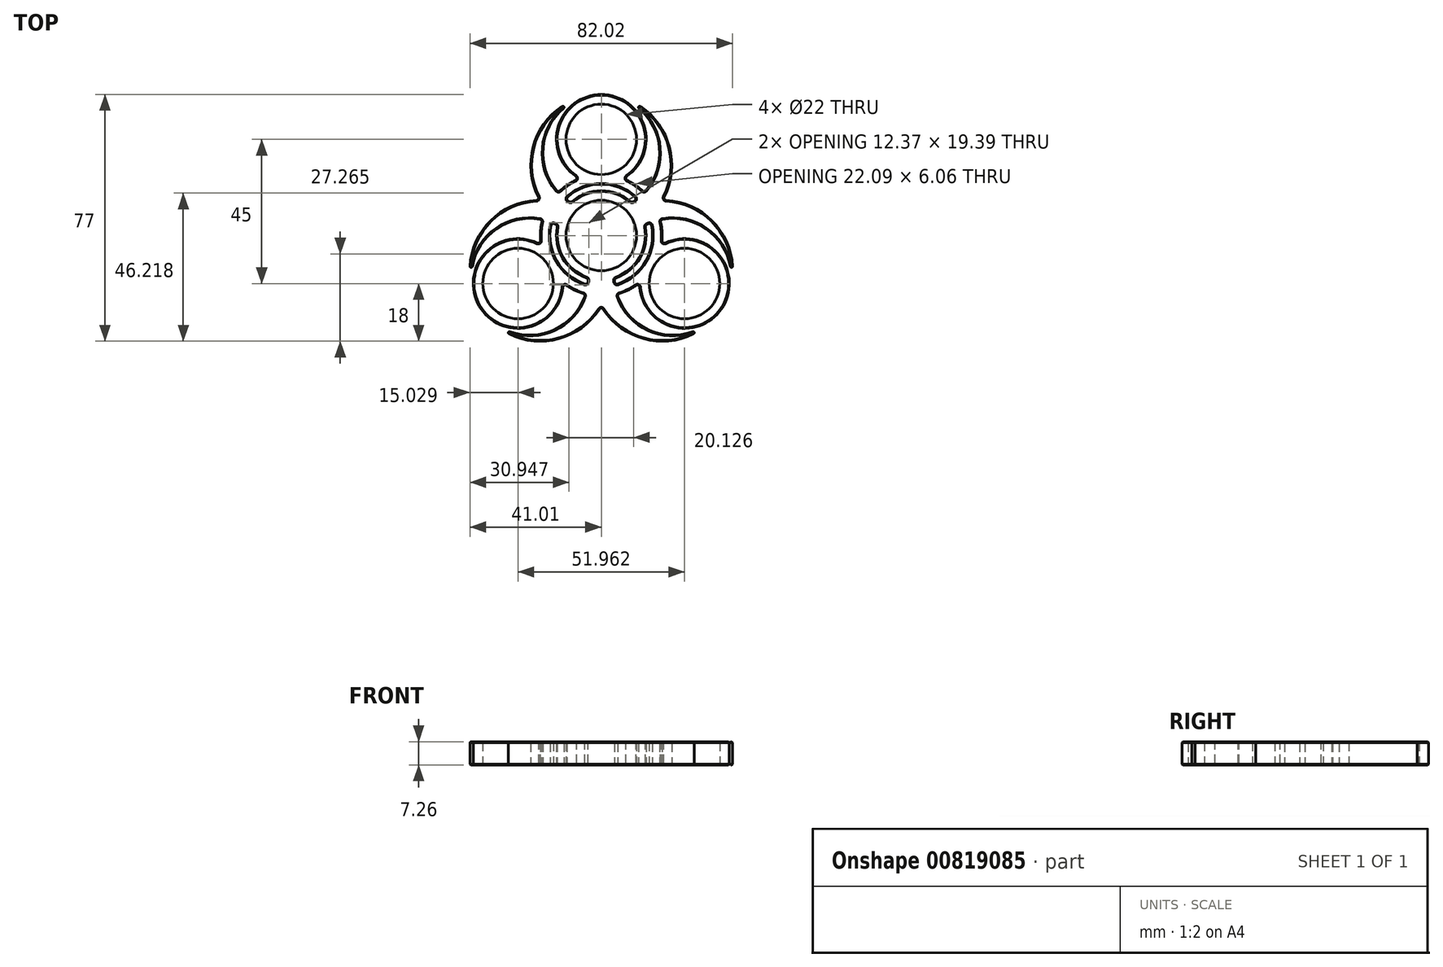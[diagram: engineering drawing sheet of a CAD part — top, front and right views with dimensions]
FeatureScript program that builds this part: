
annotation { "Feature Type Name" : "Feature", "Feature Type Description" : "" }
export const myFeature = defineFeature(function(context is Context, id is Id, definition is map)
    precondition{}
    {
        {
            var Q0;
            Q0=qCreatedBy(makeId("Top.planeOp"),FACE);
            var sketch = newSketch(context, id + "F0", { "sketchPlane" : qUnion([Q0])});
            skCircle(sketch, "E0", {"center": v(0, 0) * mm, "radius": 14 * mm});
            skCircle(sketch, "E1", {"center": v(0, 0) * mm, "radius": 11 * mm});
            skCircle(sketch, "E2", {"center": v(0, 30) * mm, "radius": 14 * mm});
            skCircle(sketch, "E3", {"center": v(0, 30) * mm, "radius": 11 * mm});
            skCircle(sketch, "E4", {"center": v(0, 0) * mm, "radius": 19 * mm});
            skCircle(sketch, "E5", {"center": v(0, 0) * mm, "radius": 16 * mm});
            skCircle(sketch, "E6.1.0", {"center": v(-25.98, -15) * mm, "radius": 14 * mm});
            skCircle(sketch, "E6.1.1", {"center": v(-25.98, -15) * mm, "radius": 11 * mm});
            skCircle(sketch, "E6.2.0", {"center": v(25.98, -15) * mm, "radius": 14 * mm});
            skCircle(sketch, "E6.2.1", {"center": v(25.98, -15) * mm, "radius": 11 * mm});
            skSolve(sketch);
        }
        {
            var Q0;
            Q0=makeQuery(id+"F0.imprint","IMPRINT",FACE,{"disambiguationData":[TD([[makeQuery(id+"F0.imprint","IMPRINT",EDGE,{"derivedFrom":sQuery(id+"F0.wireOp",EDGE,"E0")}),1.0]])]});
            var Q1;
            {var subQ0=sQuery(id+"F0.wireOp",EDGE,"E4");var subQ1=sQuery(id+"F0.wireOp",EDGE,"E2");var subQ2=makeQuery(id+"F0.imprint","INTERSECT",VERTEX,{"disambiguationData":[OD(1.0)],"derivedFrom":[subQ1,subQ0]});Q1=makeQuery(id+"F0.imprint","IMPRINT",FACE,{"disambiguationData":[TD([[makeQuery(id+"F0.imprint","IMPRINT",EDGE,{"disambiguationData":[TD([[subQ2,1.0]])],"derivedFrom":subQ1}),-1.0]])]});}
            var Q2;
            {var subQ0=sQuery(id+"F0.wireOp",EDGE,"E4");var subQ1=sQuery(id+"F0.wireOp",EDGE,"E2");var subQ2=makeQuery(id+"F0.imprint","INTERSECT",VERTEX,{"disambiguationData":[OD(0.0)],"derivedFrom":[subQ1,subQ0]});Q2=makeQuery(id+"F0.imprint","IMPRINT",FACE,{"disambiguationData":[TD([[makeQuery(id+"F0.imprint","IMPRINT",EDGE,{"disambiguationData":[TD([[subQ2,-1.0]])],"derivedFrom":subQ1}),-1.0]])]});}
            var Q3;
            {var subQ0=sQuery(id+"F0.wireOp",EDGE,"E6.1.0");var subQ1=sQuery(id+"F0.wireOp",EDGE,"E4");var subQ2=makeQuery(id+"F0.imprint","INTERSECT",VERTEX,{"disambiguationData":[OD(1.0)],"derivedFrom":[subQ1,subQ0]});Q3=makeQuery(id+"F0.imprint","IMPRINT",FACE,{"disambiguationData":[TD([[makeQuery(id+"F0.imprint","IMPRINT",EDGE,{"disambiguationData":[TD([[subQ2,-1.0]])],"derivedFrom":subQ1}),1.0]])]});}
            var Q4;
            {var subQ3=sQuery(id+"F0.wireOp",EDGE,"E6.1.1");Q4=makeQuery(id+"F0.imprint","IMPRINT",FACE,{"disambiguationData":[TD([[makeQuery(id+"F0.imprint","IMPRINT",EDGE,{"derivedFrom":subQ3}),-1.0]])]});}
            var Q5;
            {var subQ0=sQuery(id+"F0.wireOp",EDGE,"E6.1.0");var subQ1=sQuery(id+"F0.wireOp",EDGE,"E4");var subQ2=makeQuery(id+"F0.imprint","INTERSECT",VERTEX,{"disambiguationData":[OD(0.0)],"derivedFrom":[subQ1,subQ0]});Q5=makeQuery(id+"F0.imprint","IMPRINT",FACE,{"disambiguationData":[TD([[makeQuery(id+"F0.imprint","IMPRINT",EDGE,{"disambiguationData":[TD([[subQ2,-1.0]])],"derivedFrom":subQ1}),1.0]])]});}
            var Q6;
            {var subQ3=sQuery(id+"F0.wireOp",EDGE,"E6.2.1");Q6=makeQuery(id+"F0.imprint","IMPRINT",FACE,{"disambiguationData":[TD([[makeQuery(id+"F0.imprint","IMPRINT",EDGE,{"derivedFrom":subQ3}),-1.0]])]});}
            var Q7;
            {var subQ0=sQuery(id+"F0.wireOp",EDGE,"E6.2.0");var subQ1=sQuery(id+"F0.wireOp",EDGE,"E4");var subQ2=makeQuery(id+"F0.imprint","INTERSECT",VERTEX,{"disambiguationData":[OD(0.0)],"derivedFrom":[subQ1,subQ0]});Q7=makeQuery(id+"F0.imprint","IMPRINT",FACE,{"disambiguationData":[TD([[makeQuery(id+"F0.imprint","IMPRINT",EDGE,{"disambiguationData":[TD([[subQ2,-1.0]])],"derivedFrom":subQ1}),1.0]])]});}
            var Q8;
            {var subQ4=sQuery(id+"F0.wireOp",EDGE,"E3");Q8=makeQuery(id+"F0.imprint","IMPRINT",FACE,{"disambiguationData":[TD([[makeQuery(id+"F0.imprint","IMPRINT",EDGE,{"derivedFrom":subQ4}),-1.0]])]});}
            var Q9;
            {var subQ0=sQuery(id+"F0.wireOp",EDGE,"E4");var subQ1=sQuery(id+"F0.wireOp",EDGE,"E2");var subQ2=makeQuery(id+"F0.imprint","INTERSECT",VERTEX,{"disambiguationData":[OD(0.0)],"derivedFrom":[subQ1,subQ0]});Q9=makeQuery(id+"F0.imprint","IMPRINT",FACE,{"disambiguationData":[TD([[makeQuery(id+"F0.imprint","IMPRINT",EDGE,{"disambiguationData":[TD([[subQ2,-1.0]])],"derivedFrom":subQ1}),1.0]])]});}
            extrude(context, id + "F1", {"entities" : qUnion([Q0, Q1, Q2, Q3, Q4, Q5, Q6, Q7, Q8, Q9]), "endBound" : BoundingType.SYMMETRIC, "depth" : 7.25 * mm, "offsetDistance" : 25.4 * mm});
        }
        {
            var Q0;
            Q0=qCreatedBy(makeId("Top.planeOp"),FACE);
            var sketch = newSketch(context, id + "F2", { "sketchPlane" : qUnion([Q0])});
            skArc(sketch, "E7", {"start": v(-11.76, 39.7) * mm, "mid": v(0, 7.55) * mm, "end": v(11.76, 39.7) * mm});
            skLineSegment(sketch, "E8", {"start": v(12.89, 12.89) * mm, "end": v(47.12, 47.12) * mm, "construction": true});
            skArc(sketch, "E9", {"start": v(-12.2, 40.3) * mm, "mid": v(-21.42, 27) * mm, "end": v(-19.05, 11) * mm});
            skArc(sketch, "E10", {"start": v(12.2, 40.3) * mm, "mid": v(11.7, 40.21) * mm, "end": v(11.76, 39.7) * mm});
            skArc(sketch, "E11", {"start": v(-11.76, 39.7) * mm, "mid": v(-11.7, 40.21) * mm, "end": v(-12.2, 40.3) * mm});
            skArc(sketch, "E12.1.0", {"start": v(-28.5, -30.03) * mm, "mid": v(-6.54, -3.77) * mm, "end": v(-40.26, -9.67) * mm});
            skArc(sketch, "E12.1.1", {"start": v(-28.8, -30.72) * mm, "mid": v(-12.67, -32.06) * mm, "end": v(0, -22) * mm});
            skArc(sketch, "E12.1.2", {"start": v(-41, -9.58) * mm, "mid": v(-40.68, -9.98) * mm, "end": v(-40.26, -9.67) * mm});
            skArc(sketch, "E12.1.3", {"start": v(-28.5, -30.03) * mm, "mid": v(-28.98, -30.24) * mm, "end": v(-28.8, -30.72) * mm});
            skArc(sketch, "E12.2.0", {"start": v(40.26, -9.67) * mm, "mid": v(6.54, -3.77) * mm, "end": v(28.5, -30.03) * mm});
            skArc(sketch, "E12.2.1", {"start": v(41, -9.58) * mm, "mid": v(34.1, 5.05) * mm, "end": v(19.05, 11) * mm});
            skArc(sketch, "E12.2.2", {"start": v(28.8, -30.72) * mm, "mid": v(28.98, -30.24) * mm, "end": v(28.5, -30.03) * mm});
            skArc(sketch, "E12.2.3", {"start": v(40.26, -9.67) * mm, "mid": v(40.68, -9.98) * mm, "end": v(41, -9.58) * mm});
            skPoint(sketch, "E12.center", {"position": v(0, 0) * mm});
            skArc(sketch, "E13.trimOffspring", {"start": v(-19.05, 11) * mm, "mid": v(-34.1, 5.05) * mm, "end": v(-41, -9.58) * mm});
            skArc(sketch, "E14.trimOffspring", {"start": v(0, -22) * mm, "mid": v(12.67, -32.06) * mm, "end": v(28.8, -30.72) * mm});
            skArc(sketch, "E15.trimOffspring", {"start": v(19.05, 11) * mm, "mid": v(21.42, 27) * mm, "end": v(12.2, 40.3) * mm});
            skSolve(sketch);
        }
        {
            var Q0;
            Q0=makeQuery(id+"F2.imprint","IMPRINT",FACE,{"disambiguationData":[TD([[makeQuery(id+"F2.imprint","IMPRINT",EDGE,{"derivedFrom":sQuery(id+"F2.wireOp",EDGE,"E7")}),-1.0]])]});
            extrude(context, id + "F3", {"entities" : qUnion([Q0]), "operationType" : NewBodyOperationType.ADD, "endBound" : BoundingType.SYMMETRIC, "depth" : 7.25 * mm, "offsetDistance" : 25 * mm});
        }
        {
            var Q0;
            Q0=makeQuery(id+"F0.imprint","IMPRINT",FACE,{"disambiguationData":[TD([[makeQuery(id+"F0.imprint","IMPRINT",EDGE,{"derivedFrom":sQuery(id+"F0.wireOp",EDGE,"E1")}),1.0]])]});
            extrude(context, id + "F4", {"entities" : qUnion([Q0]), "operationType" : NewBodyOperationType.REMOVE, "endBound" : BoundingType.SYMMETRIC, "depth" : 8 * mm, "offsetDistance" : 25 * mm});
        }
        {
            var Q0;
            {var subQ0=sQuery(id+"F0.wireOp",EDGE,"E4");var subQ1=sQuery(id+"F0.wireOp",EDGE,"E2");Q0=makeQuery(id+"F1.opExtrude","SWEPT_EDGE",EDGE,{"disambiguationData":[OSD([subQ1,subQ0]),TDD([makeQuery(id+"F0.imprint","INTERSECT",VERTEX,{"disambiguationData":[OD(1.0)],"derivedFrom":[subQ1,subQ0]})])]});}
            var Q1;
            {var subQ0=sQuery(id+"F0.wireOp",EDGE,"E4");var subQ1=sQuery(id+"F0.wireOp",EDGE,"E2");Q1=makeQuery(id+"F1.opExtrude","SWEPT_EDGE",EDGE,{"disambiguationData":[OSD([subQ1,subQ0]),TDD([makeQuery(id+"F0.imprint","INTERSECT",VERTEX,{"disambiguationData":[OD(0.0)],"derivedFrom":[subQ1,subQ0]})])]});}
            var Q2;
            {var subQ0=sQuery(id+"F0.wireOp",EDGE,"E4");Q2=makeQuery(id+"F3.boolean.opBoolean","INTERSECT",EDGE,{"derivedFrom":[makeQuery(id+"F1.opExtrude","SWEPT_FACE",FACE,{"disambiguationData":[OSD([subQ0]),TDD([makeQuery(id+"F0.imprint","IMPRINT",EDGE,{"disambiguationData":[TD([[makeQuery(id+"F0.imprint","INTERSECT",VERTEX,{"disambiguationData":[OD(0.0)],"derivedFrom":[sQuery(id+"F0.wireOp",EDGE,"E2"),subQ0]}),-1.0]])],"derivedFrom":subQ0})])]}),makeQuery(id+"F3.opExtrude","SWEPT_FACE",FACE,{"disambiguationData":[OSD([sQuery(id+"F2.wireOp",EDGE,"E7")])]})]});}
            var Q3;
            {var subQ0=sQuery(id+"F0.wireOp",EDGE,"E4");Q3=makeQuery(id+"F3.boolean.opBoolean","INTERSECT",EDGE,{"derivedFrom":[makeQuery(id+"F1.opExtrude","SWEPT_FACE",FACE,{"disambiguationData":[OSD([subQ0]),TDD([makeQuery(id+"F0.imprint","IMPRINT",EDGE,{"disambiguationData":[TD([[makeQuery(id+"F0.imprint","INTERSECT",VERTEX,{"disambiguationData":[OD(0.0)],"derivedFrom":[sQuery(id+"F0.wireOp",EDGE,"E2"),subQ0]}),-1.0]])],"derivedFrom":subQ0})])]}),makeQuery(id+"F3.opExtrude","SWEPT_FACE",FACE,{"disambiguationData":[OSD([sQuery(id+"F2.wireOp",EDGE,"E12.1.0")])]})]});}
            var Q4;
            Q4=makeQuery(id+"F3.boolean.opBoolean","INTERSECT",EDGE,{"disambiguationData":[OD(0.0)],"derivedFrom":[makeQuery(id+"F1.opExtrude","SWEPT_FACE",FACE,{"disambiguationData":[OSD([sQuery(id+"F0.wireOp",EDGE,"E0")])]}),makeQuery(id+"F3.opExtrude","SWEPT_FACE",FACE,{"disambiguationData":[OSD([sQuery(id+"F2.wireOp",EDGE,"E12.1.0")])]})]});
            var Q5;
            Q5=makeQuery(id+"F3.boolean.opBoolean","INTERSECT",EDGE,{"disambiguationData":[OD(0.0)],"derivedFrom":[makeQuery(id+"F1.opExtrude","SWEPT_FACE",FACE,{"disambiguationData":[OSD([sQuery(id+"F0.wireOp",EDGE,"E5")])]}),makeQuery(id+"F3.opExtrude","SWEPT_FACE",FACE,{"disambiguationData":[OSD([sQuery(id+"F2.wireOp",EDGE,"E7")])]})]});
            var Q6;
            Q6=makeQuery(id+"F3.boolean.opBoolean","INTERSECT",EDGE,{"disambiguationData":[OD(0.0)],"derivedFrom":[makeQuery(id+"F1.opExtrude","SWEPT_FACE",FACE,{"disambiguationData":[OSD([sQuery(id+"F0.wireOp",EDGE,"E5")])]}),makeQuery(id+"F3.opExtrude","SWEPT_FACE",FACE,{"disambiguationData":[OSD([sQuery(id+"F2.wireOp",EDGE,"E12.1.0")])]})]});
            var Q7;
            Q7=makeQuery(id+"F3.boolean.opBoolean","INTERSECT",EDGE,{"disambiguationData":[OD(1.0)],"derivedFrom":[makeQuery(id+"F1.opExtrude","SWEPT_FACE",FACE,{"disambiguationData":[OSD([sQuery(id+"F0.wireOp",EDGE,"E5")])]}),makeQuery(id+"F3.opExtrude","SWEPT_FACE",FACE,{"disambiguationData":[OSD([sQuery(id+"F2.wireOp",EDGE,"E7")])]})]});
            var Q8;
            Q8=makeQuery(id+"F3.boolean.opBoolean","INTERSECT",EDGE,{"disambiguationData":[OD(1.0)],"derivedFrom":[makeQuery(id+"F1.opExtrude","SWEPT_FACE",FACE,{"disambiguationData":[OSD([sQuery(id+"F0.wireOp",EDGE,"E0")])]}),makeQuery(id+"F3.opExtrude","SWEPT_FACE",FACE,{"disambiguationData":[OSD([sQuery(id+"F2.wireOp",EDGE,"E7")])]})]});
            var Q9;
            Q9=makeQuery(id+"F3.boolean.opBoolean","INTERSECT",EDGE,{"disambiguationData":[OD(1.0)],"derivedFrom":[makeQuery(id+"F1.opExtrude","SWEPT_FACE",FACE,{"disambiguationData":[OSD([sQuery(id+"F0.wireOp",EDGE,"E0")])]}),makeQuery(id+"F3.opExtrude","SWEPT_FACE",FACE,{"disambiguationData":[OSD([sQuery(id+"F2.wireOp",EDGE,"E12.2.0")])]})]});
            var Q10;
            Q10=makeQuery(id+"F3.boolean.opBoolean","INTERSECT",EDGE,{"disambiguationData":[OD(1.0)],"derivedFrom":[makeQuery(id+"F1.opExtrude","SWEPT_FACE",FACE,{"disambiguationData":[OSD([sQuery(id+"F0.wireOp",EDGE,"E5")])]}),makeQuery(id+"F3.opExtrude","SWEPT_FACE",FACE,{"disambiguationData":[OSD([sQuery(id+"F2.wireOp",EDGE,"E12.2.0")])]})]});
            var Q11;
            {var subQ0=sQuery(id+"F0.wireOp",EDGE,"E4");Q11=makeQuery(id+"F3.boolean.opBoolean","INTERSECT",EDGE,{"derivedFrom":[makeQuery(id+"F1.opExtrude","SWEPT_FACE",FACE,{"disambiguationData":[OSD([subQ0]),TDD([makeQuery(id+"F0.imprint","IMPRINT",EDGE,{"disambiguationData":[TD([[makeQuery(id+"F0.imprint","INTERSECT",VERTEX,{"disambiguationData":[OD(1.0)],"derivedFrom":[sQuery(id+"F0.wireOp",EDGE,"E2"),subQ0]}),1.0]])],"derivedFrom":subQ0})])]}),makeQuery(id+"F3.opExtrude","SWEPT_FACE",FACE,{"disambiguationData":[OSD([sQuery(id+"F2.wireOp",EDGE,"E7")])]})]});}
            var Q12;
            {var subQ0=sQuery(id+"F0.wireOp",EDGE,"E4");Q12=makeQuery(id+"F3.boolean.opBoolean","INTERSECT",EDGE,{"derivedFrom":[makeQuery(id+"F1.opExtrude","SWEPT_FACE",FACE,{"disambiguationData":[OSD([subQ0]),TDD([makeQuery(id+"F0.imprint","IMPRINT",EDGE,{"disambiguationData":[TD([[makeQuery(id+"F0.imprint","INTERSECT",VERTEX,{"disambiguationData":[OD(1.0)],"derivedFrom":[sQuery(id+"F0.wireOp",EDGE,"E2"),subQ0]}),1.0]])],"derivedFrom":subQ0})])]}),makeQuery(id+"F3.opExtrude","SWEPT_FACE",FACE,{"disambiguationData":[OSD([sQuery(id+"F2.wireOp",EDGE,"E12.2.0")])]})]});}
            var Q13;
            {var subQ0=sQuery(id+"F0.wireOp",EDGE,"E6.2.0");var subQ1=sQuery(id+"F0.wireOp",EDGE,"E4");Q13=makeQuery(id+"F1.opExtrude","SWEPT_EDGE",EDGE,{"disambiguationData":[OSD([subQ1,subQ0]),TDD([makeQuery(id+"F0.imprint","INTERSECT",VERTEX,{"disambiguationData":[OD(1.0)],"derivedFrom":[subQ1,subQ0]})])]});}
            var Q14;
            {var subQ0=sQuery(id+"F0.wireOp",EDGE,"E6.2.0");var subQ1=sQuery(id+"F0.wireOp",EDGE,"E4");Q14=makeQuery(id+"F1.opExtrude","SWEPT_EDGE",EDGE,{"disambiguationData":[OSD([subQ1,subQ0]),TDD([makeQuery(id+"F0.imprint","INTERSECT",VERTEX,{"disambiguationData":[OD(0.0)],"derivedFrom":[subQ1,subQ0]})])]});}
            var Q15;
            {var subQ0=sQuery(id+"F0.wireOp",EDGE,"E4");Q15=makeQuery(id+"F3.boolean.opBoolean","INTERSECT",EDGE,{"derivedFrom":[makeQuery(id+"F1.opExtrude","SWEPT_FACE",FACE,{"disambiguationData":[OSD([subQ0]),TDD([makeQuery(id+"F0.imprint","IMPRINT",EDGE,{"disambiguationData":[TD([[makeQuery(id+"F0.imprint","INTERSECT",VERTEX,{"disambiguationData":[OD(1.0)],"derivedFrom":[subQ0,sQuery(id+"F0.wireOp",EDGE,"E6.1.0")]}),-1.0]])],"derivedFrom":subQ0})])]}),makeQuery(id+"F3.opExtrude","SWEPT_FACE",FACE,{"disambiguationData":[OSD([sQuery(id+"F2.wireOp",EDGE,"E12.2.0")])]})]});}
            var Q16;
            Q16=makeQuery(id+"F3.boolean.opBoolean","INTERSECT",EDGE,{"disambiguationData":[OD(0.0)],"derivedFrom":[makeQuery(id+"F1.opExtrude","SWEPT_FACE",FACE,{"disambiguationData":[OSD([sQuery(id+"F0.wireOp",EDGE,"E0")])]}),makeQuery(id+"F3.opExtrude","SWEPT_FACE",FACE,{"disambiguationData":[OSD([sQuery(id+"F2.wireOp",EDGE,"E12.2.0")])]})]});
            var Q17;
            Q17=makeQuery(id+"F3.boolean.opBoolean","INTERSECT",EDGE,{"disambiguationData":[OD(1.0)],"derivedFrom":[makeQuery(id+"F1.opExtrude","SWEPT_FACE",FACE,{"disambiguationData":[OSD([sQuery(id+"F0.wireOp",EDGE,"E0")])]}),makeQuery(id+"F3.opExtrude","SWEPT_FACE",FACE,{"disambiguationData":[OSD([sQuery(id+"F2.wireOp",EDGE,"E12.1.0")])]})]});
            var Q18;
            Q18=makeQuery(id+"F3.boolean.opBoolean","INTERSECT",EDGE,{"disambiguationData":[OD(1.0)],"derivedFrom":[makeQuery(id+"F1.opExtrude","SWEPT_FACE",FACE,{"disambiguationData":[OSD([sQuery(id+"F0.wireOp",EDGE,"E5")])]}),makeQuery(id+"F3.opExtrude","SWEPT_FACE",FACE,{"disambiguationData":[OSD([sQuery(id+"F2.wireOp",EDGE,"E12.1.0")])]})]});
            var Q19;
            {var subQ0=sQuery(id+"F0.wireOp",EDGE,"E6.1.0");var subQ1=sQuery(id+"F0.wireOp",EDGE,"E4");Q19=makeQuery(id+"F1.opExtrude","SWEPT_EDGE",EDGE,{"disambiguationData":[OSD([subQ1,subQ0]),TDD([makeQuery(id+"F0.imprint","INTERSECT",VERTEX,{"disambiguationData":[OD(1.0)],"derivedFrom":[subQ1,subQ0]})])]});}
            var Q20;
            {var subQ0=sQuery(id+"F0.wireOp",EDGE,"E6.1.0");var subQ1=sQuery(id+"F0.wireOp",EDGE,"E4");Q20=makeQuery(id+"F1.opExtrude","SWEPT_EDGE",EDGE,{"disambiguationData":[OSD([subQ1,subQ0]),TDD([makeQuery(id+"F0.imprint","INTERSECT",VERTEX,{"disambiguationData":[OD(0.0)],"derivedFrom":[subQ1,subQ0]})])]});}
            var Q21;
            {var subQ0=sQuery(id+"F0.wireOp",EDGE,"E4");Q21=makeQuery(id+"F3.boolean.opBoolean","INTERSECT",EDGE,{"derivedFrom":[makeQuery(id+"F1.opExtrude","SWEPT_FACE",FACE,{"disambiguationData":[OSD([subQ0]),TDD([makeQuery(id+"F0.imprint","IMPRINT",EDGE,{"disambiguationData":[TD([[makeQuery(id+"F0.imprint","INTERSECT",VERTEX,{"disambiguationData":[OD(1.0)],"derivedFrom":[subQ0,sQuery(id+"F0.wireOp",EDGE,"E6.1.0")]}),-1.0]])],"derivedFrom":subQ0})])]}),makeQuery(id+"F3.opExtrude","SWEPT_FACE",FACE,{"disambiguationData":[OSD([sQuery(id+"F2.wireOp",EDGE,"E12.1.0")])]})]});}
            var Q22;
            Q22=makeQuery(id+"F3.boolean.opBoolean","INTERSECT",EDGE,{"disambiguationData":[OD(0.0)],"derivedFrom":[makeQuery(id+"F1.opExtrude","SWEPT_FACE",FACE,{"disambiguationData":[OSD([sQuery(id+"F0.wireOp",EDGE,"E0")])]}),makeQuery(id+"F3.opExtrude","SWEPT_FACE",FACE,{"disambiguationData":[OSD([sQuery(id+"F2.wireOp",EDGE,"E7")])]})]});
            var Q23;
            Q23=makeQuery(id+"F3.opExtrude","SWEPT_EDGE",EDGE,{"disambiguationData":[OSD([sQuery(id+"F2.wireOp",EDGE,"E12.2.1"),sQuery(id+"F2.wireOp",EDGE,"E15.trimOffspring")])]});
            var Q24;
            Q24=makeQuery(id+"F3.opExtrude","SWEPT_EDGE",EDGE,{"disambiguationData":[OSD([sQuery(id+"F2.wireOp",EDGE,"E9"),sQuery(id+"F2.wireOp",EDGE,"E13.trimOffspring")])]});
            var Q25;
            Q25=makeQuery(id+"F3.opExtrude","SWEPT_EDGE",EDGE,{"disambiguationData":[OSD([sQuery(id+"F2.wireOp",EDGE,"E12.1.1"),sQuery(id+"F2.wireOp",EDGE,"E14.trimOffspring")])]});
            var Q26;
            Q26=makeQuery(id+"F3.boolean.opBoolean","INTERSECT",EDGE,{"disambiguationData":[OD(0.0)],"derivedFrom":[makeQuery(id+"F1.opExtrude","SWEPT_FACE",FACE,{"disambiguationData":[OSD([sQuery(id+"F0.wireOp",EDGE,"E5")])]}),makeQuery(id+"F3.opExtrude","SWEPT_FACE",FACE,{"disambiguationData":[OSD([sQuery(id+"F2.wireOp",EDGE,"E12.2.0")])]})]});
            fillet(context, id + "F5", {"entities" : qUnion([Q0, Q1, Q2, Q3, Q4, Q5, Q6, Q7, Q8, Q9, Q10, Q11, Q12, Q13, Q14, Q15, Q16, Q17, Q18, Q19, Q20, Q21, Q22, Q23, Q24, Q25, Q26]), "radius" : .75 * mm, "tangentPropagation" : true, "allowEdgeOverflow" : false});
        }
        {
            var Q0;
            Q0=makeQuery(id+"F3.opExtrude","CAP_EDGE",EDGE,{"disambiguationData":[OSD([sQuery(id+"F2.wireOp",EDGE,"E15.trimOffspring")])],"isStart":false});
            var Q1;
            Q1=makeQuery(id+"F3.opExtrude","CAP_EDGE",EDGE,{"disambiguationData":[OSD([sQuery(id+"F2.wireOp",EDGE,"E15.trimOffspring")])],"isStart":true});
            var Q2;
            {var subQ0=sQuery(id+"F2.wireOp",EDGE,"E7");var subQ1=sQuery(id+"F0.wireOp",EDGE,"E5");Q2=makeQuery(id+"F3.boolean.opBoolean","SPLIT",EDGE,{"disambiguationData":[TD([makeQuery(id+"F3.opExtrude","SWEPT_FACE",FACE,{"disambiguationData":[OSD([subQ0])]})])],"derivedFrom":makeQuery(id+"F1.opExtrude","CAP_EDGE",EDGE,{"disambiguationData":[OSD([subQ1])],"isStart":true})});}
            var Q3;
            {var subQ0=sQuery(id+"F2.wireOp",EDGE,"E12.1.0");var subQ1=sQuery(id+"F0.wireOp",EDGE,"E5");Q3=makeQuery(id+"F3.boolean.opBoolean","SPLIT",EDGE,{"disambiguationData":[TD([makeQuery(id+"F3.opExtrude","SWEPT_FACE",FACE,{"disambiguationData":[OSD([subQ0])]})])],"derivedFrom":makeQuery(id+"F1.opExtrude","CAP_EDGE",EDGE,{"disambiguationData":[OSD([subQ1])],"isStart":true})});}
            var Q4;
            {var subQ0=sQuery(id+"F2.wireOp",EDGE,"E12.2.0");var subQ1=sQuery(id+"F0.wireOp",EDGE,"E5");Q4=makeQuery(id+"F3.boolean.opBoolean","SPLIT",EDGE,{"disambiguationData":[TD([makeQuery(id+"F3.opExtrude","SWEPT_FACE",FACE,{"disambiguationData":[OSD([subQ0])]})])],"derivedFrom":makeQuery(id+"F1.opExtrude","CAP_EDGE",EDGE,{"disambiguationData":[OSD([subQ1])],"isStart":true})});}
            var Q5;
            {var subQ0=sQuery(id+"F2.wireOp",EDGE,"E7");var subQ1=sQuery(id+"F0.wireOp",EDGE,"E5");Q5=makeQuery(id+"F3.boolean.opBoolean","SPLIT",EDGE,{"disambiguationData":[TD([makeQuery(id+"F3.opExtrude","SWEPT_FACE",FACE,{"disambiguationData":[OSD([subQ0])]})])],"derivedFrom":makeQuery(id+"F1.opExtrude","CAP_EDGE",EDGE,{"disambiguationData":[OSD([subQ1])],"isStart":false})});}
            var Q6;
            {var subQ0=sQuery(id+"F2.wireOp",EDGE,"E12.1.0");var subQ1=sQuery(id+"F0.wireOp",EDGE,"E5");Q6=makeQuery(id+"F3.boolean.opBoolean","SPLIT",EDGE,{"disambiguationData":[TD([makeQuery(id+"F3.opExtrude","SWEPT_FACE",FACE,{"disambiguationData":[OSD([subQ0])]})])],"derivedFrom":makeQuery(id+"F1.opExtrude","CAP_EDGE",EDGE,{"disambiguationData":[OSD([subQ1])],"isStart":false})});}
            var Q7;
            {var subQ0=sQuery(id+"F2.wireOp",EDGE,"E12.2.0");var subQ1=sQuery(id+"F0.wireOp",EDGE,"E5");Q7=makeQuery(id+"F3.boolean.opBoolean","SPLIT",EDGE,{"disambiguationData":[TD([makeQuery(id+"F3.opExtrude","SWEPT_FACE",FACE,{"disambiguationData":[OSD([subQ0])]})])],"derivedFrom":makeQuery(id+"F1.opExtrude","CAP_EDGE",EDGE,{"disambiguationData":[OSD([subQ1])],"isStart":false})});}
            chamfer(context, id + "F6", {"entities" : qUnion([Q0, Q1, Q2, Q3, Q4, Q5, Q6, Q7]), "width" : .25 * mm, "tangentPropagation" : true});
        }
    });
